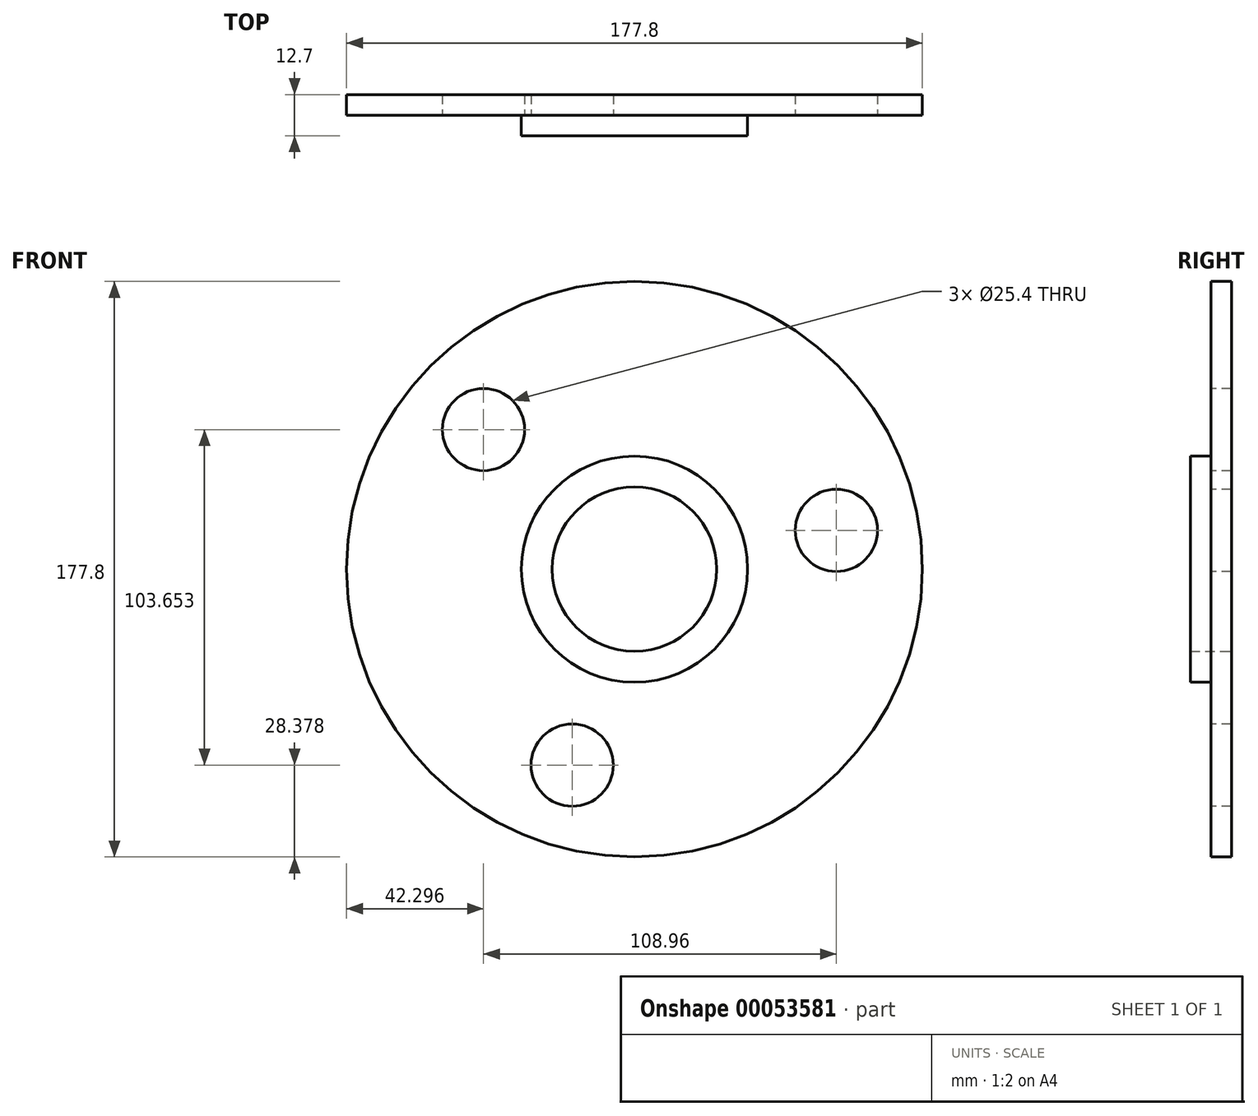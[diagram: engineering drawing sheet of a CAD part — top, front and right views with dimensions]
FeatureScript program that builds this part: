
annotation { "Feature Type Name" : "Feature", "Feature Type Description" : "" }
export const myFeature = defineFeature(function(context is Context, id is Id, definition is map)
    precondition{}
    {
        {
            var Q0;
            Q0=qCreatedBy(makeId("Front.planeOp"),FACE);
            var sketch = newSketch(context, id + "F0", { "sketchPlane" : qUnion([Q0])});
            skCircle(sketch, "E0", {"center": v(0, 0) * mm, "radius": 88.9 * mm});
            skCircle(sketch, "E1", {"center": v(0, 0) * mm, "radius": 25.4 * mm});
            skSolve(sketch);
        }
        {
            var Q0;
            Q0=makeQuery(id+"F0.imprint","IMPRINT",FACE,{"disambiguationData":[TD([[makeQuery(id+"F0.imprint","IMPRINT",EDGE,{"derivedFrom":sQuery(id+"F0.wireOp",EDGE,"E0")}),1.0]])]});
            extrude(context, id + "F1", {"entities" : qUnion([Q0]), "depth" : 6.35 * mm});
        }
        {
            var Q0;
            Q0=makeQuery(id+"F1.opExtrude","CAP_FACE",FACE,{"disambiguationData":[OSD([sQuery(id+"F0.wireOp",EDGE,"E0"),sQuery(id+"F0.wireOp",EDGE,"E1")])],"isStart":false});
            var sketch = newSketch(context, id + "F2", { "sketchPlane" : qUnion([Q0])});
            skCircle(sketch, "E2", {"center": v(0, 0) * mm, "radius": 63.5 * mm});
            skCircle(sketch, "E3", {"center": v(-46.6, 43.13) * mm, "radius": 12.7 * mm});
            skCircle(sketch, "E4", {"center": v(-19.22, -60.52) * mm, "radius": 12.7 * mm});
            skCircle(sketch, "E5", {"center": v(62.36, 12) * mm, "radius": 12.7 * mm});
            skSolve(sketch);
        }
        {
            var Q0;
            Q0=sQuery(id+"F2.wireOp",VERTEX,"E3.center");
            var Q1;
            Q1=sQuery(id+"F2.wireOp",VERTEX,"E5.center");
            var Q2;
            Q2=sQuery(id+"F2.wireOp",VERTEX,"E4.center");
            var Q3;
            Q3=makeQuery(id+"F1.opExtrude","SWEPT_BODY",BODY,{"disambiguationData":[OSD([sQuery(id+"F0.wireOp",EDGE,"E0"),sQuery(id+"F0.wireOp",EDGE,"E1")])]});
            hole(context, id + "F3", {"style" : HoleStyle.SIMPLE, "holeDiameter" : 25.4 * mm, "endStyle" : HoleEndStyle.THROUGH, "locations" : qUnion([Q0, Q1, Q2]), "scope" : qUnion([Q3])});
        }
        {
            var Q0;
            Q0=makeQuery(id+"F1.opExtrude","CAP_FACE",FACE,{"disambiguationData":[OSD([sQuery(id+"F0.wireOp",EDGE,"E0"),sQuery(id+"F0.wireOp",EDGE,"E1")])],"isStart":false});
            var sketch = newSketch(context, id + "F4", { "sketchPlane" : qUnion([Q0])});
            skCircle(sketch, "E6", {"center": v(0, 0) * mm, "radius": 34.93 * mm});
            skSolve(sketch);
        }
        {
            var Q0;
            Q0=makeQuery(id+"F4.imprint","IMPRINT",FACE,{"disambiguationData":[TD([[makeQuery(id+"F4.imprint","IMPRINT",EDGE,{"derivedFrom":sQuery(id+"F4.wireOp",EDGE,"E6")}),1.0]])]});
            extrude(context, id + "F5", {"entities" : qUnion([Q0]), "operationType" : NewBodyOperationType.ADD, "depth" : 6.35 * mm});
        }
    });
